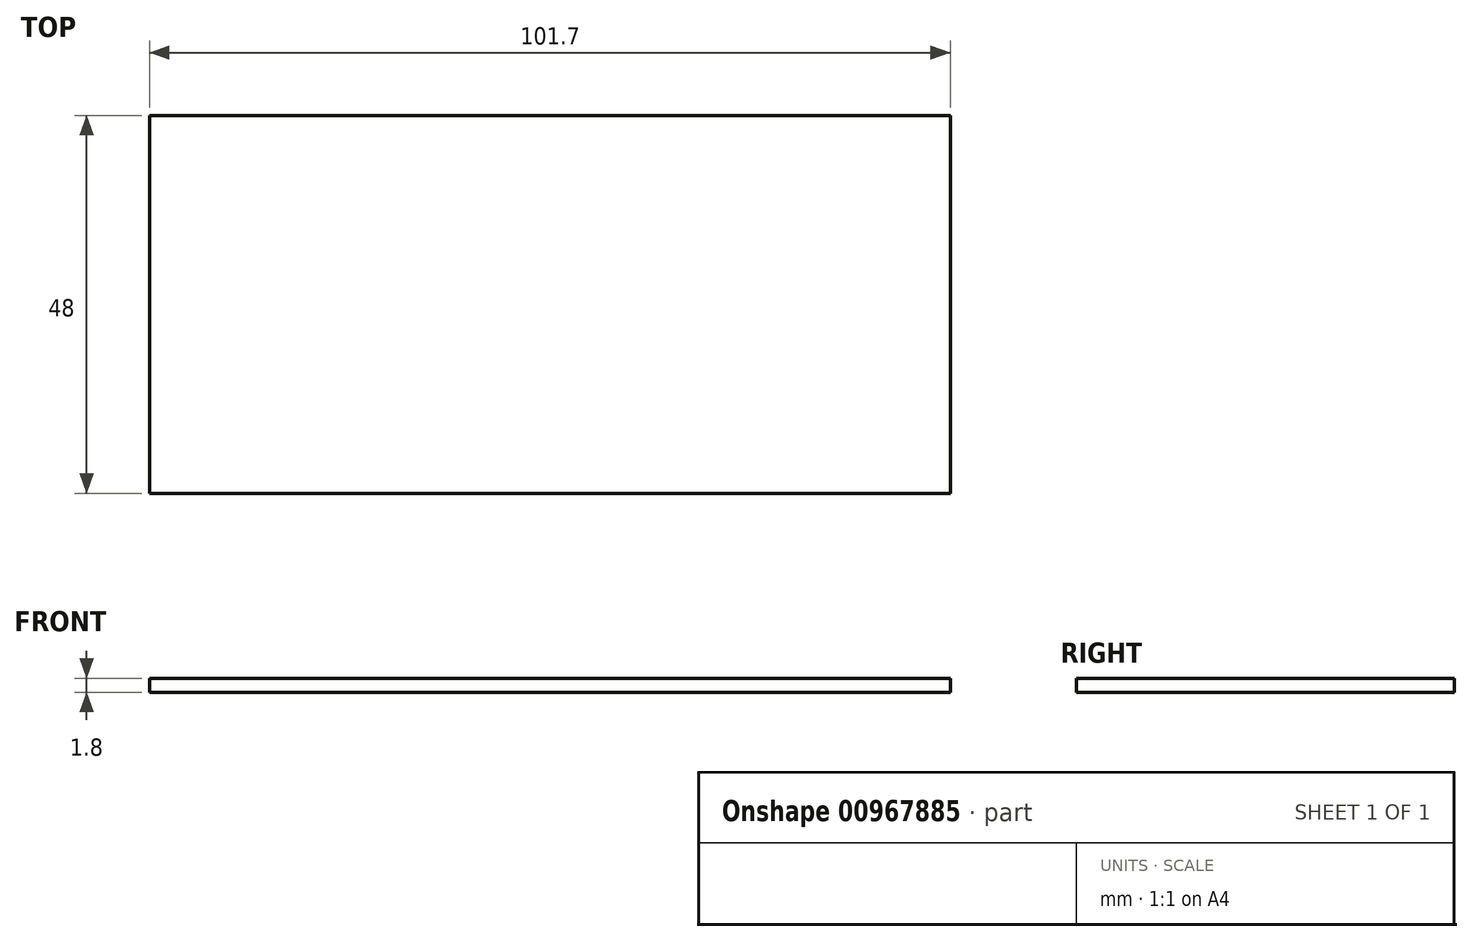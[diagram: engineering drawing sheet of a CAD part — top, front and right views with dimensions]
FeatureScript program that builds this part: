
annotation { "Feature Type Name" : "Feature", "Feature Type Description" : "" }
export const myFeature = defineFeature(function(context is Context, id is Id, definition is map)
    precondition{}
    {
        {
            var Q0;
            Q0=qCreatedBy(makeId("Top.planeOp"),FACE);
            var sketch = newSketch(context, id + "F0", { "sketchPlane" : qUnion([Q0])});
            skLineSegment(sketch, "E0.bottom", {"start": v(50.85, -24) * mm, "end": v(-50.85, -24) * mm});
            skLineSegment(sketch, "E0.top", {"start": v(50.85, 24) * mm, "end": v(-50.85, 24) * mm});
            skLineSegment(sketch, "E0.left", {"start": v(50.85, -24) * mm, "end": v(50.85, 24) * mm});
            skLineSegment(sketch, "E0.right", {"start": v(-50.85, -24) * mm, "end": v(-50.85, 24) * mm});
            skPoint(sketch, "E0.middle", {"position": v(0, 0) * mm});
            skSolve(sketch);
        }
        {
            var Q0;
            Q0 = qSketchRegion(id + "F0", true);
            extrude(context, id + "F1", {"entities" : qUnion([Q0]), "depth" : 1.8 * mm, "offsetDistance" : 25 * mm});
        }
    });
